# Revit family: ElectricalEquipment_Hager_TPNLighting&Power_TPNDB
name_source: partatom
category: Electrical Equipment
revit_build: Autodesk Revit 2015 (Build: 20160512_1515(x64)
units: mm (PartAtom-declared; Revit-internal decimal feet)

## types (3) — shared parameters
Busbar Rating = 125 A
CE Approval = Yes
Default Elevation = 1200 mm
Design Country = China
Door = 46 mm  [stored 0.150919 ft]
Frequency = 50 Hz
Location of Manufacturer = Telford, TF1 7FT
MCB Rating = 63 A
Mains Type = 3 phase
Manufacturer = Hager UK Ltd
Manufacturer Country = United Kingdom
Manufacturer Website = www.hager.co.uk
Max #3 Pole Breakers = 4
Neutral Rating = 100.00%
Number of Poles = 3
Outging Ways (TP) = 4
Packaging Recyclable = Yes
Pollution Degree = 2
Product Family = TPN-DB
Product Group = Panelboards
Product Literature = www.hager.co.uk/?artnr=JK104BG
Reference Standard = BS EN 61439-3
Shape = Rectangular
Supply Phase = 1,3
Type = ElectricalFixture
URL = www.hager.co.uk
Ui Rating = 690 V
Uimp Rating = 4000 V
Voltage = 415
Warranty ID = 24 Months

## per-type parameters (varying)
| type | Colour | Description | Door Type | EAN | Enclosure Rating | Hager Catalogue Ref | Location | Model | Overall Height | Overall Width | Packaging Weight | Product Description | Product Range | Product Weight | Revision | Show Door |
| TPN DB 125A 04 Way GD with door | BS4800:2011 00A01 Oyster Grey | JK1 TPN B Board 4x 63A TP Ways DB Glazed Door | Single Glazed Door | 5015652250234 | IP3X | JK104BG | Indoors | JK104BG | 133 mm  [stored 0.436352 ft] | 465 mm  [stored 1.52559 ft] | 1.00 kg | JK1 TPN B Board 4x 63A TP Ways DB Glazed Door | Invicta 3 TPN DB Type B | 8.80 kg | 3 | Yes |
| TPN DB 125A 04 Way IP65 GRP | RAL 7035 Light Grey | JK1 TPN B Board 4x 63A TP Ways DB Glazed Door | Single Glazed Door | 5015652251507 | IP65 | JK104BF | Outdoors | JK104BF | 300 mm | 600 mm | 2.00 kg | JK1 TPN B Board 4x 63A TP Ways DB Glazed Door | Invicta 3 TPN DB Type B 125A IP65 Insulated | 24.90 kg | 0 | No |
| TPN DB 125A 04 Way IP65 Metal | RAL 7035 Light Grey | TPN DB 125A 04 Way IP65 Metal | Single Plain Door | 5015652251484 | IP65 | JK104BD | Indoors | JK104BD | 300 mm | 600 mm | 2.00 kg | TPN DB 125A 04 Way IP65 Metal | TPN DB 125A 04 Way IP65 Metal | 33.10 kg | 0 | No |

note: [stored X ft] marks values corroborated as IEEE doubles in the binary element streams (Revit-internal decimal feet)

## geometry (parser evidence)
native form markers: Sweep x3
no freeform markers — native parametric forms only
